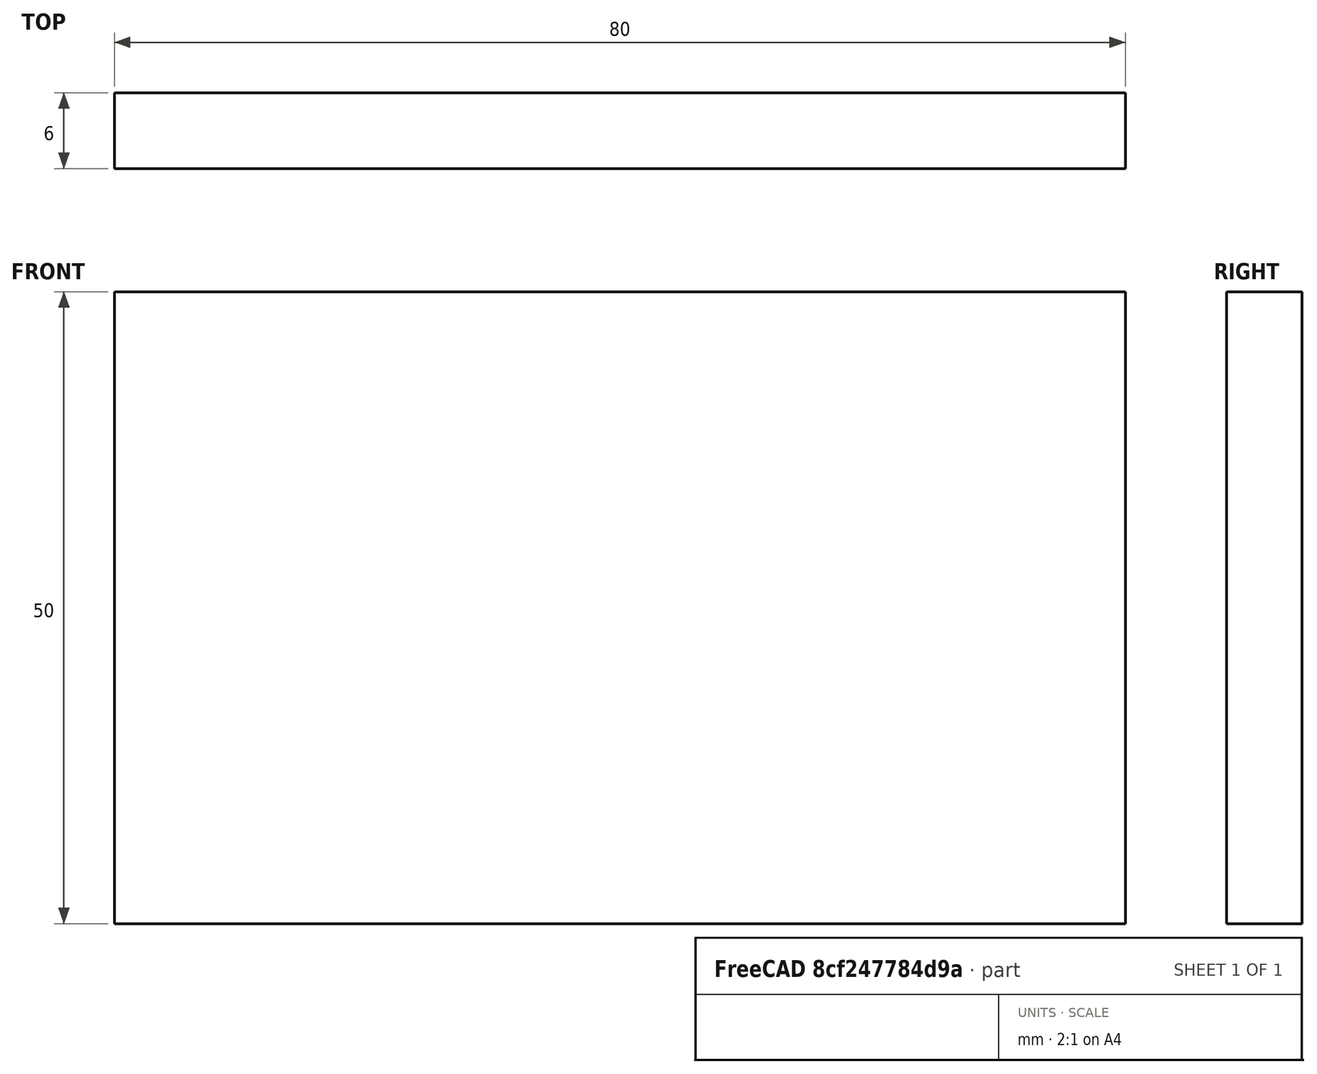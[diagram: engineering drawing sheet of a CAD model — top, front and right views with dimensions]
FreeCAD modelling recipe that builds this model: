
FCSTD DOCUMENT  (FreeCAD 0.15R4671 (Git))
Label: Flat Bar 80x6 EN10058 S235JR
License: All rights reserved
LicenseURL: http://en.wikipedia.org/wiki/All_rights_reserved
objects: Sketcher::SketchObject×1, Part::Extrusion×1
note: 2 computed .brp shape members not serialized (recipe doc carries the construction recipe); baked Part::Feature solids carry a one-line shape summary decoded from their .brp

FEATURE [Sketcher::SketchObject] Sketch
  sketch-geometry (4):
    g0: LineSegment StartX=-40 StartY=-3 StartZ=0 EndX=40 EndY=-3 EndZ=0
    g1: LineSegment StartX=40 StartY=-3 StartZ=0 EndX=40 EndY=3 EndZ=0
    g2: LineSegment StartX=40 StartY=3 StartZ=0 EndX=-40 EndY=3 EndZ=0
    g3: LineSegment StartX=-40 StartY=3 StartZ=0 EndX=-40 EndY=-3 EndZ=0
  constraints (12):
    c: Coincident(g0,g1)
    c: Coincident(g1,g2)
    c: Coincident(g2,g3)
    c: Coincident(g3,g0)
    c: Horizontal(g0)
    c: Horizontal(g2)
    c: Vertical(g1)
    c: Vertical(g3)
    c: Symmetric(g1,g2,g-2)
    c: Symmetric(g0,g1,g-1)
    c: DistanceY(g1) = 6
    c: DistanceX(g0) = 80
FEATURE [Part::Extrusion] Extrude  label="Flat Bar 80x6 EN10058 S235JR"
  Base = -> Sketch
  Dir = (0,0,50)
  Solid = true
